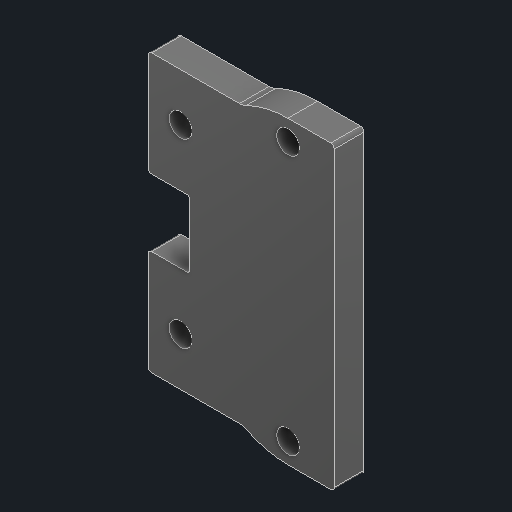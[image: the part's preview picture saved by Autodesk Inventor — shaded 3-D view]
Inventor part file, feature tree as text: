
AUTODESK INVENTOR PART (.ipt)
format: ipt  version: 2025 (Build 290162000, 162)  size: 111,616 bytes
history: native  units: in
note: dims shown in document units (in); Inventor stores cm internally (conversion verified against a paired STEP export)
features: fillet x1
ambient origin geometry x8: Origin, YZ Plane, XZ Plane, XY Plane, X Axis, Y Axis, Z Axis, Center Point
bodies: Solid1 (feature_tree)
feature tree (1):
  fillet  "Fillet1"  [1 undecoded]
note: 1 required parameter value undecoded (feature->parameter linkage not recoverable at this tier; creation-order binding heuristic only, values carry confidence <= 0.55)
